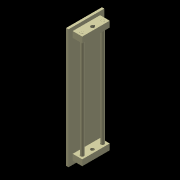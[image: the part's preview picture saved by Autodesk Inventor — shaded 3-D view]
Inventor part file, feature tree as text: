
AUTODESK INVENTOR PART (.ipt)
format: ipt  version: 2020 (Build 240168000, 168)  size: 158,208 bytes
history: native  units: mm
features: extrude x6, projected_geometry x2, other x1, thread x1, plane x1, mirror x1
ambient origin geometry x8: Origin, YZ Plane, XZ Plane, XY Plane, X Axis, Y Axis, Z Axis, Center Point
bodies: Body1 (feature_tree)
feature tree (12):
  other  "實體1"
  extrude  "Extrusion1"  Depth=3.0mm
  extrude  "Extrusion11"  Depth=6.0mm
  thread  "Thread2"  [1 undecoded]
  plane  "Work Plane3"
  extrude  "Extrusion13"  Depth=12.0mm
  mirror  "Mirror2"
  extrude  "Extrusion14"  Depth=1.0mm
  extrude  "Extrusion15"  Depth=2.0mm TaperAngle=0.0deg
  extrude  "Extrusion16"  Depth=10.0mm TaperAngle=0.0deg
  projected_geometry  "Projected Loop6"
  projected_geometry  "Projected Loop7"
note: 1 required parameter value undecoded (feature->parameter linkage not recoverable at this tier; creation-order binding heuristic only, values carry confidence <= 0.55)
